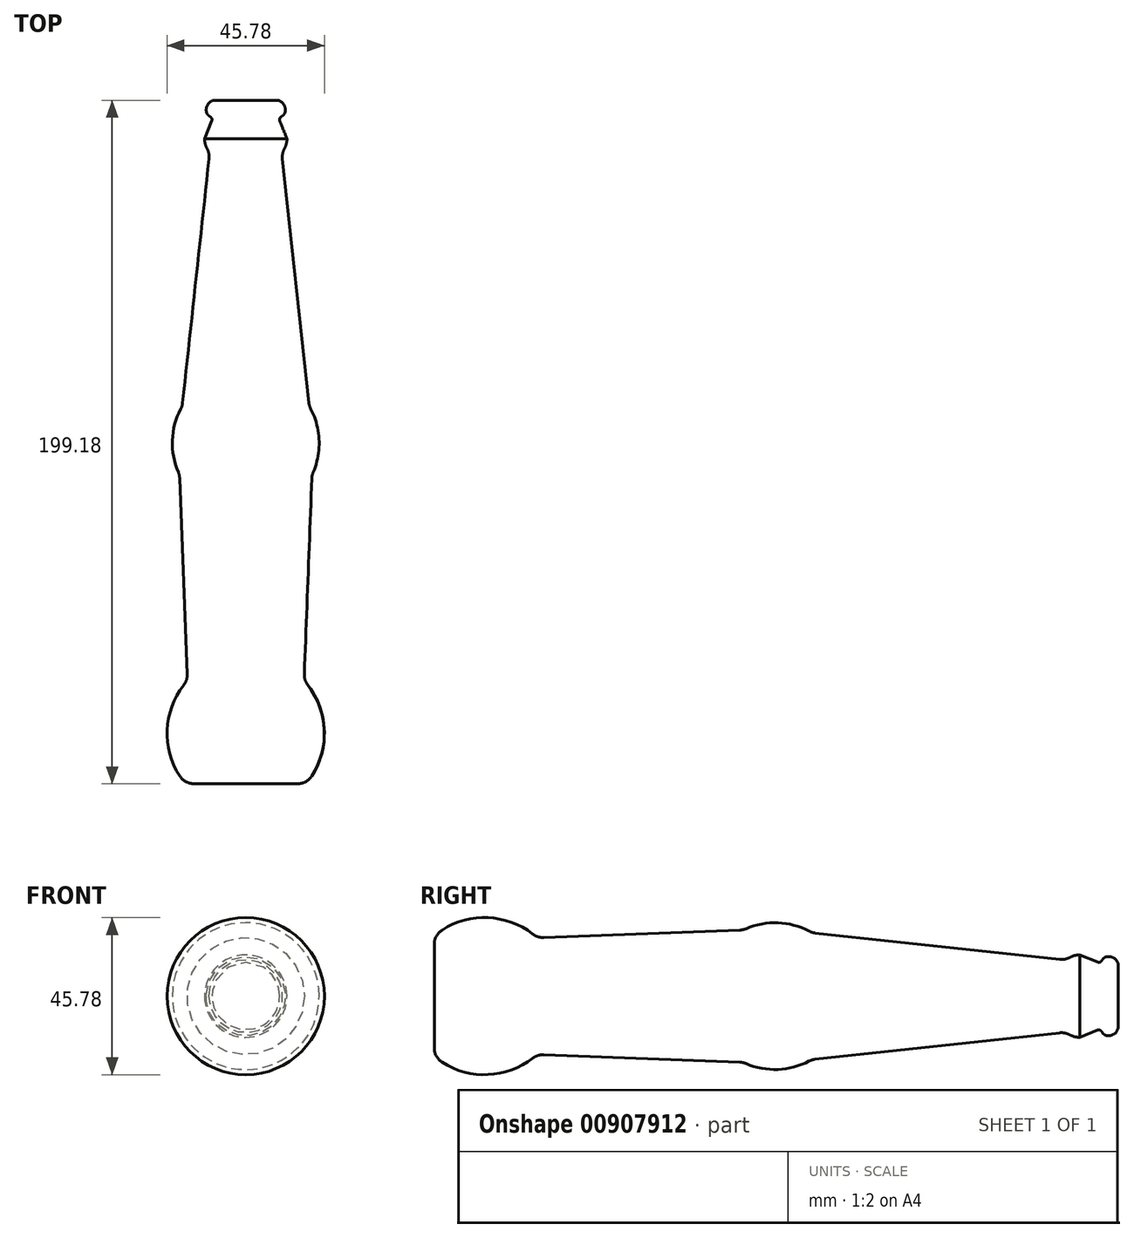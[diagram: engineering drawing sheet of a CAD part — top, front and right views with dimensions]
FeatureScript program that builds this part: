
annotation { "Feature Type Name" : "Feature", "Feature Type Description" : "" }
export const myFeature = defineFeature(function(context is Context, id is Id, definition is map)
    precondition{}
    {
        {
            var Q0;
            Q0=qCreatedBy(makeId("Top.planeOp"),FACE);
            var sketch = newSketch(context, id + "F0", { "sketchPlane" : qUnion([Q0])});
            skLineSegment(sketch, "E0", {"start": v(-82.1, -59.3) * mm, "end": v(-64.51, -59.3) * mm});
            skPoint(sketch, "E1", {"position": v(-82.1, -29.3) * mm});
            skPoint(sketch, "E2", {"position": v(-82.1, -59.3) * mm});
            skPoint(sketch, "E3", {"position": v(-82.1, 30.7) * mm});
            skPoint(sketch, "E4", {"position": v(-82.1, 50.7) * mm});
            skPoint(sketch, "E5", {"position": v(-82.1, 124.7) * mm});
            skPoint(sketch, "E6", {"position": v(-82.1, 128.67) * mm});
            skArc(sketch, "E7", {"start": v(-70.1, 128.67) * mm, "mid": v(-70.48, 126.55) * mm, "end": v(-71.6, 124.7) * mm});
            skPoint(sketch, "E8", {"position": v(-82.1, 138.67) * mm});
            skLineSegment(sketch, "E9", {"start": v(-71.6, 124.7) * mm, "end": v(-63.6, 50.7) * mm});
            skArc(sketch, "E10", {"start": v(-63.6, 50.7) * mm, "mid": v(-60.71, 40.8) * mm, "end": v(-62.8, 30.7) * mm});
            skPoint(sketch, "E11.orphan", {"position": v(-61.1, 30.7) * mm});
            skLineSegment(sketch, "E12", {"start": v(-62.8, 30.7) * mm, "end": v(-65.1, -29.3) * mm});
            skArc(sketch, "E13", {"start": v(-65.1, -29.3) * mm, "mid": v(-59.2, -44.2) * mm, "end": v(-64.51, -59.3) * mm});
            skPoint(sketch, "E14.orphan", {"position": v(-99.1, -29.3) * mm});
            skPoint(sketch, "E15.orphan", {"position": v(-102.1, -59.3) * mm});
            skPoint(sketch, "E16.orphan", {"position": v(-62.1, -59.3) * mm});
            skPoint(sketch, "E17.orphan", {"position": v(-90.1, 138.67) * mm});
            skPoint(sketch, "E18.start.orphan", {"position": v(-94.1, 128.67) * mm});
            skLineSegment(sketch, "E19", {"start": v(-70.1, 128.67) * mm, "end": v(-72.72, 135.24) * mm});
            skLineSegment(sketch, "E20", {"start": v(-72.72, 135.24) * mm, "end": v(-71.2, 135.24) * mm});
            skArc(sketch, "E21", {"start": v(-71.2, 135.24) * mm, "mid": v(-70.7, 138) * mm, "end": v(-72.76, 139.88) * mm});
            skLineSegment(sketch, "E22", {"start": v(-72.76, 139.88) * mm, "end": v(-82.1, 139.88) * mm});
            skLineSegment(sketch, "E23", {"start": v(-82.1, 139.88) * mm, "end": v(-82.1, -59.3) * mm});
            skPoint(sketch, "E24.trimOffspring.end.orphan", {"position": v(-74.1, 138.67) * mm});
            skSolve(sketch);
        }
        {
            var Q0;
            Q0=makeQuery(id+"F0.imprint","IMPRINT",FACE,{"disambiguationData":[TD([[makeQuery(id+"F0.imprint","IMPRINT",EDGE,{"derivedFrom":sQuery(id+"F0.wireOp",EDGE,"E0")}),1.0]])]});
            var Q1;
            Q1=sQuery(id+"F0.wireOp",EDGE,"E23");
            revolve(context, id + "F1", {"surfaceOperationType" : NewSurfaceOperationType.NEW, "entities" : qUnion([Q0]), "axis" : qUnion([Q1]), "revolveType" : RevolveType.FULL});
        }
        {
            var Q0;
            Q0=makeQuery(id+"F1.opRevolve","SWEPT_EDGE",EDGE,{"disambiguationData":[OSD([sQuery(id+"F0.wireOp",EDGE,"E9"),sQuery(id+"F0.wireOp",EDGE,"E10")])]});
            var Q1;
            Q1=makeQuery(id+"F1.opRevolve","SWEPT_EDGE",EDGE,{"disambiguationData":[OSD([sQuery(id+"F0.wireOp",EDGE,"E10"),sQuery(id+"F0.wireOp",EDGE,"E12")])]});
            var Q2;
            Q2=makeQuery(id+"F1.opRevolve","SWEPT_EDGE",EDGE,{"disambiguationData":[OSD([sQuery(id+"F0.wireOp",EDGE,"E12"),sQuery(id+"F0.wireOp",EDGE,"E13")])]});
            var Q3;
            Q3=makeQuery(id+"F1.opRevolve","SWEPT_EDGE",EDGE,{"disambiguationData":[OSD([sQuery(id+"F0.wireOp",EDGE,"E0"),sQuery(id+"F0.wireOp",EDGE,"E13")])]});
            var Q4;
            Q4=makeQuery(id+"F1.opRevolve","SWEPT_EDGE",EDGE,{"disambiguationData":[OSD([sQuery(id+"F0.wireOp",EDGE,"E7"),sQuery(id+"F0.wireOp",EDGE,"E9")])]});
            fillet(context, id + "F2", {"entities" : qUnion([Q0, Q1, Q2, Q3, Q4]), "radius" : 5 * mm, "tangentPropagation" : true, "allowEdgeOverflow" : false});
        }
        {
            var Q0;
            Q0=makeQuery(id+"F1.opRevolve","SWEPT_EDGE",EDGE,{"disambiguationData":[OSD([sQuery(id+"F0.wireOp",EDGE,"E19"),sQuery(id+"F0.wireOp",EDGE,"E20")])]});
            fillet(context, id + "F3", {"entities" : qUnion([Q0]), "radius" : 1 * mm, "tangentPropagation" : true, "allowEdgeOverflow" : false});
        }
        {
            var Q0;
            Q0=makeQuery(id+"F1.opRevolve","SWEPT_EDGE",EDGE,{"disambiguationData":[OSD([sQuery(id+"F0.wireOp",EDGE,"E20"),sQuery(id+"F0.wireOp",EDGE,"E21")])]});
            fillet(context, id + "F4", {"entities" : qUnion([Q0]), "radius" : 2 * mm, "tangentPropagation" : true, "allowEdgeOverflow" : false});
        }
        {
            var Q0;
            Q0=makeQuery(id+"F1.opRevolve","SWEPT_EDGE",EDGE,{"disambiguationData":[OSD([sQuery(id+"F0.wireOp",EDGE,"E21"),sQuery(id+"F0.wireOp",EDGE,"E22")])]});
            fillet(context, id + "F5", {"entities" : qUnion([Q0]), "radius" : 1 * mm, "tangentPropagation" : true, "allowEdgeOverflow" : false});
        }
    });
